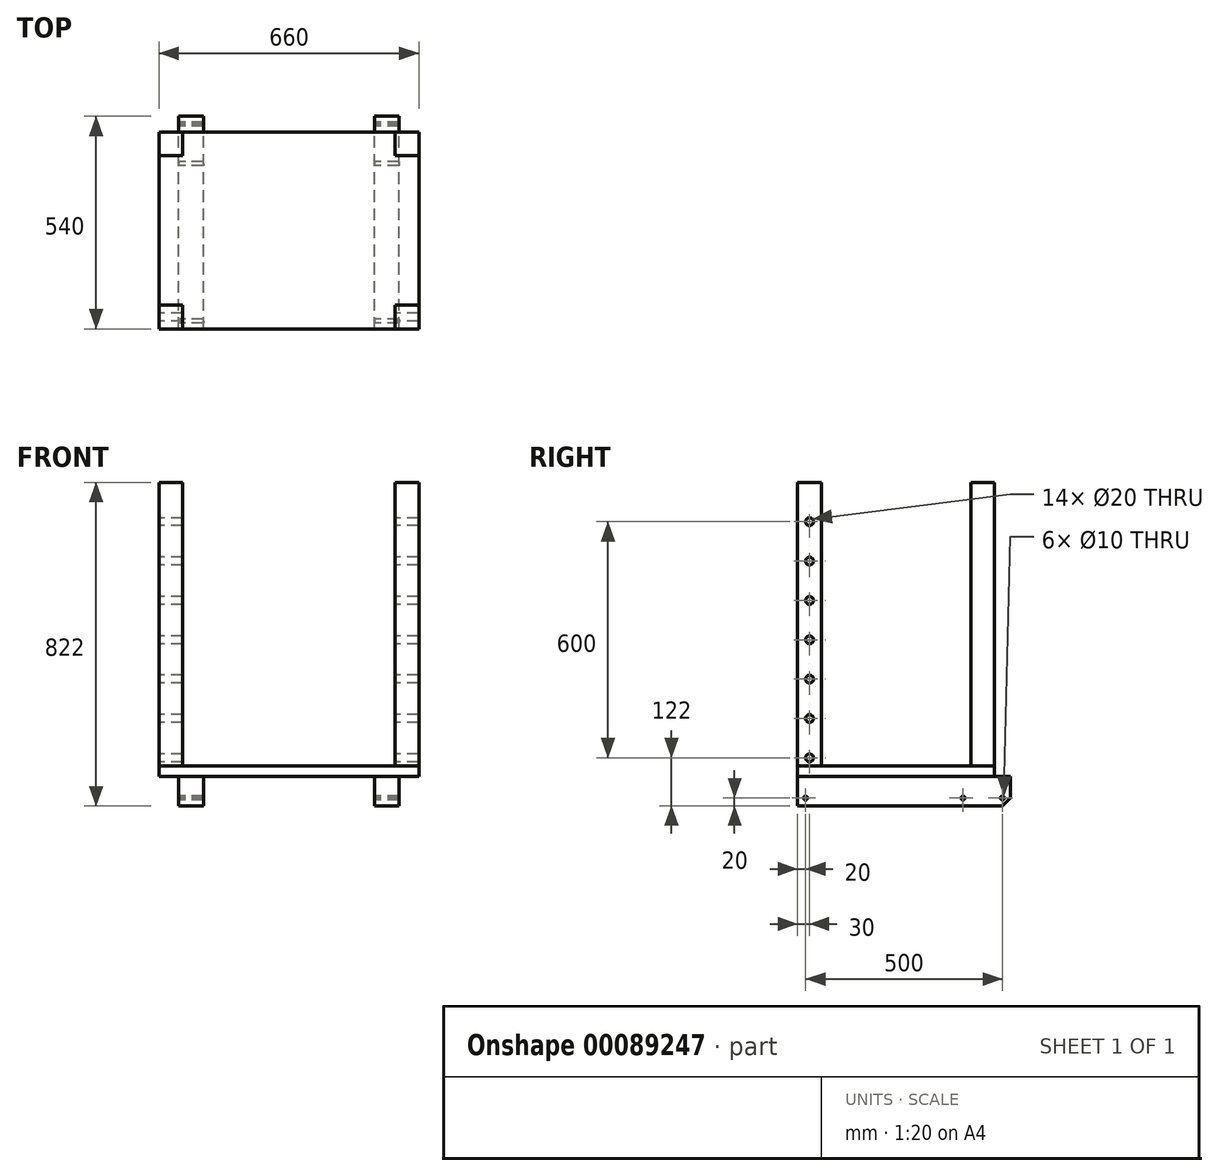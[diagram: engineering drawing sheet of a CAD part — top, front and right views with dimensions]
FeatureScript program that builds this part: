
annotation { "Feature Type Name" : "Feature", "Feature Type Description" : "" }
export const myFeature = defineFeature(function(context is Context, id is Id, definition is map)
    precondition{}
    {
        {
            var Q0;
            Q0=qCreatedBy(makeId("Top.planeOp"),FACE);
            var sketch = newSketch(context, id + "F0", { "sketchPlane" : qUnion([Q0])});
            skLineSegment(sketch, "E0.bottom", {"start": v(-330, 250) * mm, "end": v(330, 250) * mm});
            skLineSegment(sketch, "E0.top", {"start": v(-330, -250) * mm, "end": v(330, -250) * mm});
            skLineSegment(sketch, "E0.left", {"start": v(-330, 250) * mm, "end": v(-330, -250) * mm});
            skLineSegment(sketch, "E0.right", {"start": v(330, 250) * mm, "end": v(330, -250) * mm});
            skPoint(sketch, "E0.middle", {"position": v(0, 0) * mm});
            skSolve(sketch);
        }
        {
            var Q0;
            Q0=makeQuery(id+"F0.imprint","IMPRINT",FACE,{"disambiguationData":[TD([[makeQuery(id+"F0.imprint","IMPRINT",EDGE,{"derivedFrom":sQuery(id+"F0.wireOp",EDGE,"E0.bottom")}),-1.0]])]});
            extrude(context, id + "F1", {"entities" : qUnion([Q0]), "depth" : 27 * mm});
        }
        {
            var Q0;
            Q0=makeQuery(id+"F1.opExtrude","CAP_FACE",FACE,{"disambiguationData":[OSD([sQuery(id+"F0.wireOp",EDGE,"E0.bottom"),sQuery(id+"F0.wireOp",EDGE,"E0.top"),sQuery(id+"F0.wireOp",EDGE,"E0.left"),sQuery(id+"F0.wireOp",EDGE,"E0.right")])],"isStart":false});
            var sketch = newSketch(context, id + "F2", { "sketchPlane" : qUnion([Q0])});
            skLineSegment(sketch, "E1.bottom", {"start": v(-330, 250) * mm, "end": v(-270, 250) * mm});
            skLineSegment(sketch, "E1.top", {"start": v(-330, 190) * mm, "end": v(-270, 190) * mm});
            skLineSegment(sketch, "E1.left", {"start": v(-330, 250) * mm, "end": v(-330, 190) * mm});
            skLineSegment(sketch, "E1.right", {"start": v(-270, 250) * mm, "end": v(-270, 190) * mm});
            skLineSegment(sketch, "E2.bottom", {"start": v(-330, -250) * mm, "end": v(-270, -250) * mm});
            skLineSegment(sketch, "E2.top", {"start": v(-330, -190) * mm, "end": v(-270, -190) * mm});
            skLineSegment(sketch, "E2.left", {"start": v(-330, -250) * mm, "end": v(-330, -190) * mm});
            skLineSegment(sketch, "E2.right", {"start": v(-270, -250) * mm, "end": v(-270, -190) * mm});
            skLineSegment(sketch, "E3.bottom", {"start": v(330, 250) * mm, "end": v(270, 250) * mm});
            skLineSegment(sketch, "E3.top", {"start": v(330, 190) * mm, "end": v(270, 190) * mm});
            skLineSegment(sketch, "E3.left", {"start": v(330, 250) * mm, "end": v(330, 190) * mm});
            skLineSegment(sketch, "E3.right", {"start": v(270, 250) * mm, "end": v(270, 190) * mm});
            skLineSegment(sketch, "E4.bottom", {"start": v(330, -250) * mm, "end": v(270, -250) * mm});
            skLineSegment(sketch, "E4.top", {"start": v(330, -190) * mm, "end": v(270, -190) * mm});
            skLineSegment(sketch, "E4.left", {"start": v(330, -250) * mm, "end": v(330, -190) * mm});
            skLineSegment(sketch, "E4.right", {"start": v(270, -250) * mm, "end": v(270, -190) * mm});
            skSolve(sketch);
        }
        {
            var Q0;
            Q0=makeQuery(id+"F2.imprint","IMPRINT",FACE,{"disambiguationData":[TD([[makeQuery(id+"F2.imprint","IMPRINT",EDGE,{"derivedFrom":sQuery(id+"F2.wireOp",EDGE,"E1.bottom")}),-1.0]])]});
            var Q1;
            Q1=makeQuery(id+"F2.imprint","IMPRINT",FACE,{"disambiguationData":[TD([[makeQuery(id+"F2.imprint","IMPRINT",EDGE,{"derivedFrom":sQuery(id+"F2.wireOp",EDGE,"E3.bottom")}),-1.0]])]});
            var Q2;
            Q2=makeQuery(id+"F2.imprint","IMPRINT",FACE,{"disambiguationData":[TD([[makeQuery(id+"F2.imprint","IMPRINT",EDGE,{"derivedFrom":sQuery(id+"F2.wireOp",EDGE,"E4.bottom")}),1.0]])]});
            var Q3;
            Q3=makeQuery(id+"F2.imprint","IMPRINT",FACE,{"disambiguationData":[TD([[makeQuery(id+"F2.imprint","IMPRINT",EDGE,{"derivedFrom":sQuery(id+"F2.wireOp",EDGE,"E2.bottom")}),1.0]])]});
            extrude(context, id + "F3", {"entities" : qUnion([Q0, Q1, Q2, Q3]), "depth" : 720 * mm});
        }
        {
            var Q0;
            Q0=makeQuery(id+"F1.opExtrude","CAP_FACE",FACE,{"disambiguationData":[OSD([sQuery(id+"F0.wireOp",EDGE,"E0.bottom"),sQuery(id+"F0.wireOp",EDGE,"E0.top"),sQuery(id+"F0.wireOp",EDGE,"E0.left"),sQuery(id+"F0.wireOp",EDGE,"E0.right")])],"isStart":true});
            var sketch = newSketch(context, id + "F4", { "sketchPlane" : qUnion([Q0])});
            skLineSegment(sketch, "E5", {"start": v(-280, 250) * mm, "end": v(-280, -250) * mm, "construction": true});
            skLineSegment(sketch, "E6.bottom", {"start": v(-280, -187) * mm, "end": v(-217, -187) * mm});
            skLineSegment(sketch, "E6.top", {"start": v(-280, -290) * mm, "end": v(-217, -290) * mm});
            skLineSegment(sketch, "E6.left", {"start": v(-280, -187) * mm, "end": v(-280, -290) * mm});
            skLineSegment(sketch, "E6.right", {"start": v(-217, -187) * mm, "end": v(-217, -290) * mm});
            skLineSegment(sketch, "E7.bottom", {"start": v(280, -187) * mm, "end": v(217, -187) * mm});
            skLineSegment(sketch, "E7.top", {"start": v(280, -290) * mm, "end": v(217, -290) * mm});
            skLineSegment(sketch, "E7.left", {"start": v(280, -187) * mm, "end": v(280, -290) * mm});
            skLineSegment(sketch, "E7.right", {"start": v(217, -187) * mm, "end": v(217, -290) * mm});
            skLineSegment(sketch, "E8.bottom", {"start": v(280, -187) * mm, "end": v(-280, -187) * mm});
            skLineSegment(sketch, "E8.top", {"start": v(280, -154) * mm, "end": v(-280, -154) * mm});
            skLineSegment(sketch, "E8.left", {"start": v(280, -187) * mm, "end": v(280, -154) * mm});
            skLineSegment(sketch, "E8.right", {"start": v(-280, -187) * mm, "end": v(-280, -154) * mm});
            skLineSegment(sketch, "E9.bottom", {"start": v(-217, 217) * mm, "end": v(217, 217) * mm});
            skLineSegment(sketch, "E9.top", {"start": v(-280, 250) * mm, "end": v(280, 250) * mm});
            skLineSegment(sketch, "E9.left", {"start": v(-280, 217) * mm, "end": v(-280, 250) * mm});
            skLineSegment(sketch, "E9.right", {"start": v(280, 217) * mm, "end": v(280, 250) * mm});
            skLineSegment(sketch, "E10", {"start": v(280, -154) * mm, "end": v(280, 250) * mm, "construction": true});
            skLineSegment(sketch, "E11.top", {"start": v(280, -154) * mm, "end": v(217, -154) * mm});
            skLineSegment(sketch, "E11.left", {"start": v(280, 217) * mm, "end": v(280, -154) * mm});
            skLineSegment(sketch, "E11.right", {"start": v(217, 217) * mm, "end": v(217, -154) * mm});
            skLineSegment(sketch, "E12.top", {"start": v(-280, -154) * mm, "end": v(-217, -154) * mm});
            skLineSegment(sketch, "E12.left", {"start": v(-280, 217) * mm, "end": v(-280, -154) * mm});
            skLineSegment(sketch, "E12.right", {"start": v(-217, 217) * mm, "end": v(-217, -154) * mm});
            skLineSegment(sketch, "E13", {"start": v(217, -154) * mm, "end": v(217, -187) * mm});
            skLineSegment(sketch, "E14", {"start": v(-217, -154) * mm, "end": v(-217, -187) * mm});
            skLineSegment(sketch, "E15", {"start": v(217, 217) * mm, "end": v(217, 250) * mm});
            skLineSegment(sketch, "E16", {"start": v(-217, 217) * mm, "end": v(-217, 250) * mm});
            skSolve(sketch);
        }
        {
            var Q0;
            {var subQ0=sQuery(id+"F4.wireOp",EDGE,"E6.bottom");Q0=makeQuery(id+"F4.imprint","IMPRINT",FACE,{"disambiguationData":[TD([[makeQuery(id+"F4.imprint","IMPRINT",EDGE,{"derivedFrom":subQ0}),-1.0]])]});}
            var Q1;
            {var subQ0=sQuery(id+"F4.wireOp",EDGE,"E6.top");Q1=makeQuery(id+"F4.imprint","IMPRINT",FACE,{"disambiguationData":[TD([[makeQuery(id+"F4.imprint","IMPRINT",EDGE,{"derivedFrom":subQ0}),1.0]])]});}
            var Q2;
            {var subQ0=sQuery(id+"F4.wireOp",EDGE,"55c69af3-8ec9-44b8-babe-cd8922ee04610.MirrorCS");Q2=makeQuery(id+"F4.imprint","IMPRINT",FACE,{"disambiguationData":[TD([[makeQuery(id+"F4.imprint","IMPRINT",EDGE,{"derivedFrom":subQ0}),1.0]])]});}
            var Q3;
            {var subQ0=sQuery(id+"F4.wireOp",EDGE,"dc260f2c-bf93-496e-8821-7ffc03b002130.MirrorCS");Q3=makeQuery(id+"F4.imprint","IMPRINT",FACE,{"disambiguationData":[TD([[makeQuery(id+"F4.imprint","IMPRINT",EDGE,{"derivedFrom":subQ0}),-1.0]])]});}
            var Q4;
            {var subQ0=sQuery(id+"F4.wireOp",EDGE,"E7.top");Q4=makeQuery(id+"F4.imprint","IMPRINT",FACE,{"disambiguationData":[TD([[makeQuery(id+"F4.imprint","IMPRINT",EDGE,{"derivedFrom":subQ0}),-1.0]])]});}
            var Q5;
            {var subQ0=sQuery(id+"F4.wireOp",EDGE,"E7.bottom");Q5=makeQuery(id+"F4.imprint","IMPRINT",FACE,{"disambiguationData":[TD([[makeQuery(id+"F4.imprint","IMPRINT",EDGE,{"derivedFrom":subQ0}),1.0]])]});}
            var Q6;
            {var subQ0=sQuery(id+"F4.wireOp",EDGE,"E8.bottom");var subQ5=sQuery(id+"F4.wireOp",EDGE,"E7.right");var subQ6=makeQuery(id+"F4.imprint","INTERSECT",VERTEX,{"derivedFrom":[subQ5,subQ0]});Q6=makeQuery(id+"F4.imprint","IMPRINT",FACE,{"disambiguationData":[TD([[makeQuery(id+"F4.imprint","IMPRINT",EDGE,{"disambiguationData":[TD([[subQ6,-1.0]])],"derivedFrom":subQ5}),1.0]])]});}
            var Q7;
            {var subQ0=sQuery(id+"F4.wireOp",EDGE,"E8.bottom");var subQ5=sQuery(id+"F4.wireOp",EDGE,"E6.right");var subQ6=makeQuery(id+"F4.imprint","INTERSECT",VERTEX,{"derivedFrom":[subQ5,subQ0]});Q7=makeQuery(id+"F4.imprint","IMPRINT",FACE,{"disambiguationData":[TD([[makeQuery(id+"F4.imprint","IMPRINT",EDGE,{"disambiguationData":[TD([[subQ6,-1.0]])],"derivedFrom":subQ5}),-1.0]])]});}
            var Q8;
            Q8=makeQuery(id+"F4.imprint","IMPRINT",FACE,{"disambiguationData":[TD([[makeQuery(id+"F4.imprint","IMPRINT",EDGE,{"derivedFrom":sQuery(id+"F4.wireOp",EDGE,"E11.bottom")}),1.0]])]});
            var Q9;
            Q9=makeQuery(id+"F4.imprint","IMPRINT",FACE,{"disambiguationData":[TD([[makeQuery(id+"F4.imprint","IMPRINT",EDGE,{"derivedFrom":sQuery(id+"F4.wireOp",EDGE,"E12.bottom")}),-1.0]])]});
            var Q10;
            {var subQ0=sQuery(id+"F4.wireOp",EDGE,"E9.right");Q10=makeQuery(id+"F4.imprint","IMPRINT",FACE,{"disambiguationData":[TD([[makeQuery(id+"F4.imprint","IMPRINT",EDGE,{"derivedFrom":subQ0}),1.0]])]});}
            var Q11;
            {var subQ0=sQuery(id+"F4.wireOp",EDGE,"E9.left");Q11=makeQuery(id+"F4.imprint","IMPRINT",FACE,{"disambiguationData":[TD([[makeQuery(id+"F4.imprint","IMPRINT",EDGE,{"derivedFrom":subQ0}),-1.0]])]});}
            var Q12;
            {var subQ0=sQuery(id+"F4.wireOp",EDGE,"E8.left");Q12=makeQuery(id+"F4.imprint","IMPRINT",FACE,{"disambiguationData":[TD([[makeQuery(id+"F4.imprint","IMPRINT",EDGE,{"derivedFrom":subQ0}),1.0]])]});}
            var Q13;
            {var subQ0=sQuery(id+"F4.wireOp",EDGE,"E8.right");Q13=makeQuery(id+"F4.imprint","IMPRINT",FACE,{"disambiguationData":[TD([[makeQuery(id+"F4.imprint","IMPRINT",EDGE,{"derivedFrom":subQ0}),-1.0]])]});}
            var Q14;
            {var subQ4=sQuery(id+"F4.wireOp",EDGE,"E11.right");Q14=makeQuery(id+"F4.imprint","IMPRINT",FACE,{"disambiguationData":[TD([[makeQuery(id+"F4.imprint","IMPRINT",EDGE,{"derivedFrom":subQ4}),1.0]])]});}
            var Q15;
            {var subQ0=sQuery(id+"F4.wireOp",EDGE,"E13");Q15=makeQuery(id+"F4.imprint","IMPRINT",FACE,{"disambiguationData":[TD([[makeQuery(id+"F4.imprint","IMPRINT",EDGE,{"derivedFrom":subQ0}),1.0]])]});}
            extrude(context, id + "F5", {"entities" : qUnion([Q0, Q1, Q2, Q3, Q4, Q5, Q6, Q7, Q8, Q9, Q10, Q11, Q12, Q13, Q14, Q15]), "depth" : 75 * mm});
        }
        {
            var Q0;
            Q0=makeQuery(id+"F5.opExtrude","SWEPT_FACE",FACE,{"disambiguationData":[OSD([sQuery(id+"F4.wireOp",EDGE,"E6.left")])]});
            var sketch = newSketch(context, id + "F6", { "sketchPlane" : qUnion([Q0])});
            skCircle(sketch, "E17", {"center": v(-270, -55) * mm, "radius": 5 * mm});
            skSolve(sketch);
        }
        {
            var Q0;
            Q0=makeQuery(id+"F6.imprint","IMPRINT",FACE,{"disambiguationData":[TD([[makeQuery(id+"F6.imprint","IMPRINT",EDGE,{"derivedFrom":sQuery(id+"F6.wireOp",EDGE,"E17")}),1.0]])]});
            extrude(context, id + "F7", {"entities" : qUnion([Q0]), "operationType" : NewBodyOperationType.REMOVE, "endBound" : BoundingType.THROUGH_ALL, "oppositeDirection" : true, "depth" : 25 * mm});
        }
        {
            var Q0;
            Q0=makeQuery(id+"F3.boolean.opBoolean","MERGE",FACE,{"derivedFrom":[makeQuery(id+"F1.opExtrude","SWEPT_FACE",FACE,{"disambiguationData":[OSD([sQuery(id+"F0.wireOp",EDGE,"E0.left")])]}),makeQuery(id+"F3.opExtrude","SWEPT_FACE",FACE,{"disambiguationData":[OSD([sQuery(id+"F2.wireOp",EDGE,"E1.left")])]}),makeQuery(id+"F3.opExtrude","SWEPT_FACE",FACE,{"disambiguationData":[OSD([sQuery(id+"F2.wireOp",EDGE,"E2.left")])]})]});
            var sketch = newSketch(context, id + "F8", { "sketchPlane" : qUnion([Q0])});
            skLineSegment(sketch, "E18", {"start": v(220, 747) * mm, "end": v(220, 0) * mm, "construction": true});
            skCircle(sketch, "E19", {"center": v(220, 647) * mm, "radius": 10 * mm});
            skCircle(sketch, "E20.MirrorC", {"center": v(-220, 647) * mm, "radius": 10 * mm});
            skCircle(sketch, "E21.0.1.0", {"center": v(220, 547) * mm, "radius": 10 * mm});
            skCircle(sketch, "E21.0.2.0", {"center": v(220, 447) * mm, "radius": 10 * mm});
            skCircle(sketch, "E21.0.3.0", {"center": v(220, 347) * mm, "radius": 10 * mm});
            skCircle(sketch, "E21.0.4.0", {"center": v(220, 247) * mm, "radius": 10 * mm});
            skCircle(sketch, "E21.0.5.0", {"center": v(220, 147) * mm, "radius": 10 * mm});
            skCircle(sketch, "E21.0.6.0", {"center": v(220, 47) * mm, "radius": 10 * mm});
            skLineSegment(sketch, "E21.direction1", {"start": v(220, 647) * mm, "end": v(245, 647) * mm, "construction": true});
            skLineSegment(sketch, "E21.direction2", {"start": v(220, 647) * mm, "end": v(220, 547) * mm, "construction": true});
            skCircle(sketch, "E22.MirrorC", {"center": v(-220, 547) * mm, "radius": 10 * mm});
            skCircle(sketch, "E23.MirrorC", {"center": v(-220, 447) * mm, "radius": 10 * mm});
            skCircle(sketch, "E24.MirrorC", {"center": v(-220, 347) * mm, "radius": 10 * mm});
            skCircle(sketch, "E25.MirrorC", {"center": v(-220, 247) * mm, "radius": 10 * mm});
            skCircle(sketch, "E26.MirrorC", {"center": v(-220, 147) * mm, "radius": 10 * mm});
            skCircle(sketch, "E27.MirrorC", {"center": v(-220, 47) * mm, "radius": 10 * mm});
            skSolve(sketch);
        }
        {
            var Q0;
            Q0=makeQuery(id+"F5.opExtrude","SWEPT_FACE",FACE,{"disambiguationData":[OSD([sQuery(id+"F4.wireOp",EDGE,"E6.left"),sQuery(id+"F4.wireOp",EDGE,"E8.right"),sQuery(id+"F4.wireOp",EDGE,"E9.left"),sQuery(id+"F4.wireOp",EDGE,"E12.left")])]});
            var sketch = newSketch(context, id + "F9", { "sketchPlane" : qUnion([Q0])});
            skCircle(sketch, "E28", {"center": v(230, -55) * mm, "radius": 5 * mm});
            skCircle(sketch, "E29", {"center": v(-170, -55) * mm, "radius": 5 * mm});
            skSolve(sketch);
        }
        {
            var Q0;
            Q0=makeQuery(id+"F9.imprint","IMPRINT",FACE,{"disambiguationData":[TD([[makeQuery(id+"F9.imprint","IMPRINT",EDGE,{"derivedFrom":sQuery(id+"F9.wireOp",EDGE,"E28")}),1.0]])]});
            var Q1;
            Q1=makeQuery(id+"F9.imprint","IMPRINT",FACE,{"disambiguationData":[TD([[makeQuery(id+"F9.imprint","IMPRINT",EDGE,{"derivedFrom":sQuery(id+"F9.wireOp",EDGE,"E29")}),1.0]])]});
            extrude(context, id + "F10", {"entities" : qUnion([Q0, Q1]), "operationType" : NewBodyOperationType.REMOVE, "endBound" : BoundingType.THROUGH_ALL, "oppositeDirection" : true, "depth" : 25 * mm});
        }
        {
            var Q0;
            Q0=makeQuery(id+"F5.opExtrude","SWEPT_FACE",FACE,{"disambiguationData":[OSD([sQuery(id+"F4.wireOp",EDGE,"E6.left"),sQuery(id+"F4.wireOp",EDGE,"E8.right"),sQuery(id+"F4.wireOp",EDGE,"E9.left"),sQuery(id+"F4.wireOp",EDGE,"E12.left")])]});
            var sketch = newSketch(context, id + "F11", { "sketchPlane" : qUnion([Q0])});
            skCircle(sketch, "E30", {"center": v(-270, -55) * mm, "radius": 20 * mm, "construction": true});
            skLineSegment(sketch, "E31", {"start": v(-290, -75) * mm, "end": v(-270, -75) * mm});
            skLineSegment(sketch, "E32", {"start": v(-290, -55) * mm, "end": v(-290, -75) * mm});
            skLineSegment(sketch, "E33", {"start": v(-270, -75) * mm, "end": v(-290, -55) * mm});
            skSolve(sketch);
        }
        {
            var Q0;
            Q0=makeQuery(id+"F11.imprint","IMPRINT",FACE,{"disambiguationData":[TD([[makeQuery(id+"F11.imprint","IMPRINT",EDGE,{"derivedFrom":sQuery(id+"F11.wireOp",EDGE,"SUK3F1vi-8bPF-lZ23-fldP-WPFYDv0suV95")}),1.0]])]});
            var Q1;
            Q1=makeQuery(id+"F11.imprint","IMPRINT",FACE,{"disambiguationData":[TD([[makeQuery(id+"F11.imprint","IMPRINT",EDGE,{"derivedFrom":sQuery(id+"F11.wireOp",EDGE,"E31")}),-1.0]])]});
            extrude(context, id + "F12", {"entities" : qUnion([Q0, Q1]), "operationType" : NewBodyOperationType.REMOVE, "endBound" : BoundingType.THROUGH_ALL, "oppositeDirection" : true, "depth" : 25 * mm});
        }
        {
            var Q0;
            Q0=makeQuery(id+"F8.imprint","IMPRINT",FACE,{"disambiguationData":[TD([[makeQuery(id+"F8.imprint","IMPRINT",EDGE,{"derivedFrom":sQuery(id+"F8.wireOp",EDGE,"E19")}),1.0]])]});
            var Q1;
            Q1=makeQuery(id+"F8.imprint","IMPRINT",FACE,{"disambiguationData":[TD([[makeQuery(id+"F8.imprint","IMPRINT",EDGE,{"derivedFrom":sQuery(id+"F8.wireOp",EDGE,"E21.0.1.0")}),1.0]])]});
            var Q2;
            Q2=makeQuery(id+"F8.imprint","IMPRINT",FACE,{"disambiguationData":[TD([[makeQuery(id+"F8.imprint","IMPRINT",EDGE,{"derivedFrom":sQuery(id+"F8.wireOp",EDGE,"E21.0.2.0")}),1.0]])]});
            var Q3;
            Q3=makeQuery(id+"F8.imprint","IMPRINT",FACE,{"disambiguationData":[TD([[makeQuery(id+"F8.imprint","IMPRINT",EDGE,{"derivedFrom":sQuery(id+"F8.wireOp",EDGE,"E21.0.3.0")}),1.0]])]});
            var Q4;
            Q4=makeQuery(id+"F8.imprint","IMPRINT",FACE,{"disambiguationData":[TD([[makeQuery(id+"F8.imprint","IMPRINT",EDGE,{"derivedFrom":sQuery(id+"F8.wireOp",EDGE,"E21.0.4.0")}),1.0]])]});
            var Q5;
            Q5=makeQuery(id+"F8.imprint","IMPRINT",FACE,{"disambiguationData":[TD([[makeQuery(id+"F8.imprint","IMPRINT",EDGE,{"derivedFrom":sQuery(id+"F8.wireOp",EDGE,"E20.MirrorC")}),-1.0]])]});
            var Q6;
            Q6=makeQuery(id+"F8.imprint","IMPRINT",FACE,{"disambiguationData":[TD([[makeQuery(id+"F8.imprint","IMPRINT",EDGE,{"derivedFrom":sQuery(id+"F8.wireOp",EDGE,"E22.MirrorC")}),-1.0]])]});
            var Q7;
            Q7=makeQuery(id+"F8.imprint","IMPRINT",FACE,{"disambiguationData":[TD([[makeQuery(id+"F8.imprint","IMPRINT",EDGE,{"derivedFrom":sQuery(id+"F8.wireOp",EDGE,"E23.MirrorC")}),-1.0]])]});
            var Q8;
            Q8=makeQuery(id+"F8.imprint","IMPRINT",FACE,{"disambiguationData":[TD([[makeQuery(id+"F8.imprint","IMPRINT",EDGE,{"derivedFrom":sQuery(id+"F8.wireOp",EDGE,"E24.MirrorC")}),-1.0]])]});
            var Q9;
            Q9=makeQuery(id+"F8.imprint","IMPRINT",FACE,{"disambiguationData":[TD([[makeQuery(id+"F8.imprint","IMPRINT",EDGE,{"derivedFrom":sQuery(id+"F8.wireOp",EDGE,"E25.MirrorC")}),-1.0]])]});
            var Q10;
            Q10=makeQuery(id+"F8.imprint","IMPRINT",FACE,{"disambiguationData":[TD([[makeQuery(id+"F8.imprint","IMPRINT",EDGE,{"derivedFrom":sQuery(id+"F8.wireOp",EDGE,"E26.MirrorC")}),-1.0]])]});
            var Q11;
            Q11=makeQuery(id+"F8.imprint","IMPRINT",FACE,{"disambiguationData":[TD([[makeQuery(id+"F8.imprint","IMPRINT",EDGE,{"derivedFrom":sQuery(id+"F8.wireOp",EDGE,"E27.MirrorC")}),-1.0]])]});
            var Q12;
            Q12=makeQuery(id+"F8.imprint","IMPRINT",FACE,{"disambiguationData":[TD([[makeQuery(id+"F8.imprint","IMPRINT",EDGE,{"derivedFrom":sQuery(id+"F8.wireOp",EDGE,"E21.0.5.0")}),1.0]])]});
            var Q13;
            Q13=makeQuery(id+"F8.imprint","IMPRINT",FACE,{"disambiguationData":[TD([[makeQuery(id+"F8.imprint","IMPRINT",EDGE,{"derivedFrom":sQuery(id+"F8.wireOp",EDGE,"E21.0.6.0")}),1.0]])]});
            extrude(context, id + "F13", {"entities" : qUnion([Q0, Q1, Q2, Q3, Q4, Q5, Q6, Q7, Q8, Q9, Q10, Q11, Q12, Q13]), "operationType" : NewBodyOperationType.REMOVE, "endBound" : BoundingType.THROUGH_ALL, "oppositeDirection" : true, "depth" : 25 * mm});
        }
    });
